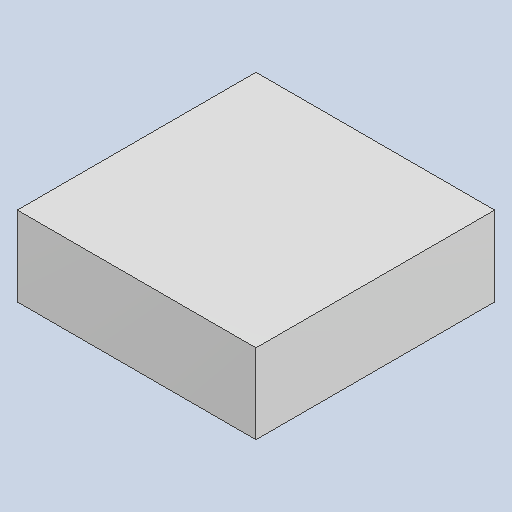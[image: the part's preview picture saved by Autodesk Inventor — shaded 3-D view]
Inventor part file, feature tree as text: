
AUTODESK INVENTOR PART (.ipt)
format: ipt  version: 2023.4 (Build 274418000, 418)  size: 79,872 bytes
history: native  units: mm
features: extrude x1
ambient origin geometry x8: Origin, YZ Plane, XZ Plane, XY Plane, X Axis, Y Axis, Z Axis, Center Point
bodies: Solid1 (feature_tree)
feature tree (1):
  extrude  "Extruded_25"  [1 undecoded]
note: 1 required parameter value undecoded (feature->parameter linkage not recoverable at this tier; creation-order binding heuristic only, values carry confidence <= 0.55)
